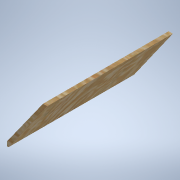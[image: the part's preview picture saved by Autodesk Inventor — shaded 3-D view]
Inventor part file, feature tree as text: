
AUTODESK INVENTOR PART (.ipt)
format: ipt  version: 2021 (Build 250183000, 183)  size: 103,424 bytes
history: native  units: in
note: dims shown in document units (in); Inventor stores cm internally (conversion verified against a paired STEP export)
features: other x4, reference x2, extrude x1, sketch x1
ambient origin geometry x8: Origin, YZ Plane, XZ Plane, XY Plane, X Axis, Y Axis, Z Axis, Center Point
bodies: Solid1 (feature_tree)
feature tree (8):
  extrude  "Extrusion1"  [1 undecoded]
  sketch  "Sketch1"  dims[d3=16.9291in d4=0.0in]
  reference  "Reference1"
  reference  "Reference2"
  other  "<userpath>\Documents\Inventor CAD\Kerbal Kontroller\v.2.iam"
  other  "v.2.iam"
  other  "Plexi:1"
  other  "Back:1"
note: 1 required parameter value undecoded (feature->parameter linkage not recoverable at this tier; creation-order binding heuristic only, values carry confidence <= 0.55)
